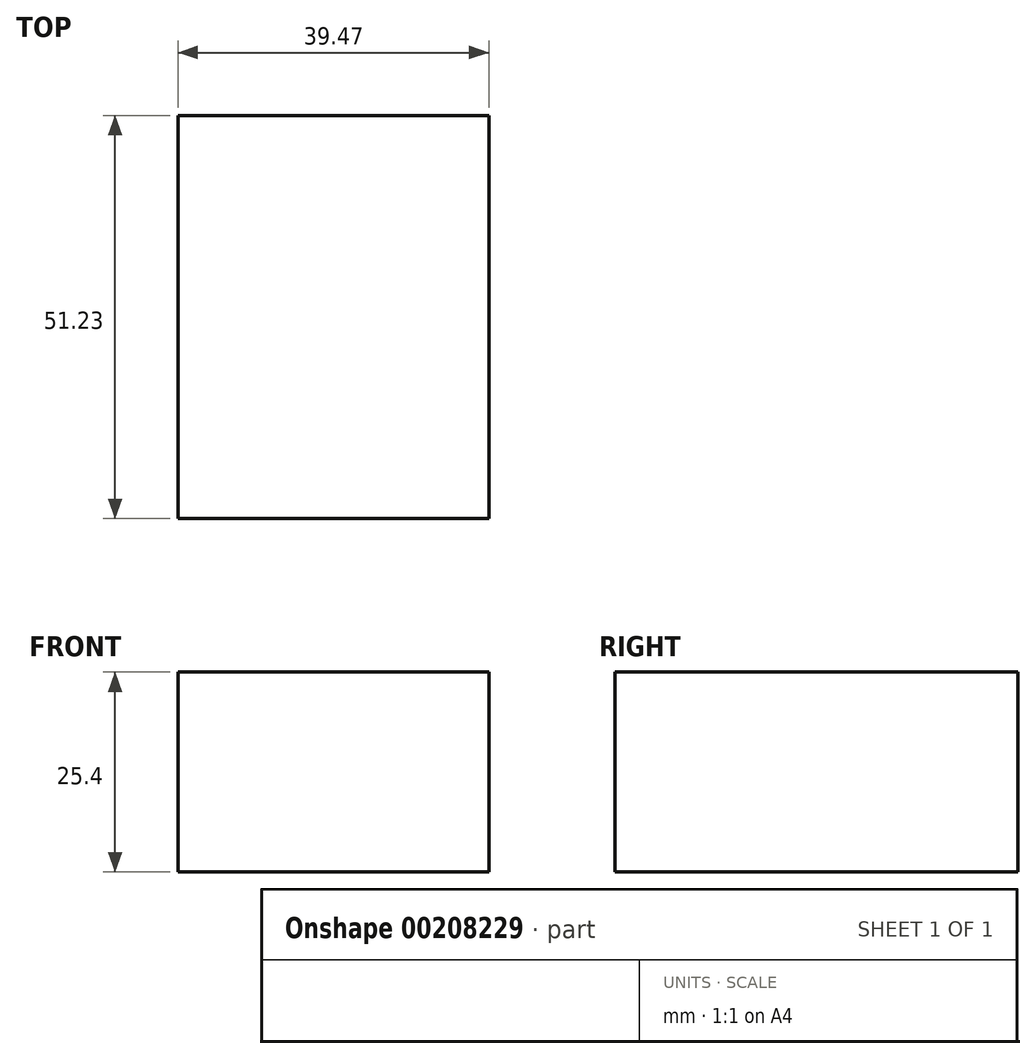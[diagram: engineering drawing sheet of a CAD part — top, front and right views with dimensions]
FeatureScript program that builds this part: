
annotation { "Feature Type Name" : "Feature", "Feature Type Description" : "" }
export const myFeature = defineFeature(function(context is Context, id is Id, definition is map)
    precondition{}
    {
        {
            var Q0;
            Q0=qCreatedBy(makeId("Top.planeOp"),FACE);
            var sketch = newSketch(context, id + "F0", { "sketchPlane" : qUnion([Q0])});
            skLineSegment(sketch, "E0.bottom", {"start": v(-20.8, 24.56) * mm, "end": v(18.68, 24.56) * mm});
            skLineSegment(sketch, "E0.top", {"start": v(-20.8, -26.67) * mm, "end": v(18.68, -26.67) * mm});
            skLineSegment(sketch, "E0.left", {"start": v(-20.8, 24.56) * mm, "end": v(-20.8, -26.67) * mm});
            skLineSegment(sketch, "E0.right", {"start": v(18.68, 24.56) * mm, "end": v(18.68, -26.67) * mm});
            skSolve(sketch);
        }
        {
            var Q0;
            Q0=makeQuery(id+"F0.imprint","IMPRINT",FACE,{"disambiguationData":[TD([[makeQuery(id+"F0.imprint","IMPRINT",EDGE,{"derivedFrom":sQuery(id+"F0.wireOp",EDGE,"E0.bottom")}),-1.0]])]});
            extrude(context, id + "F1", {"entities" : qUnion([Q0]), "depth" : 25.4 * mm});
        }
    });
